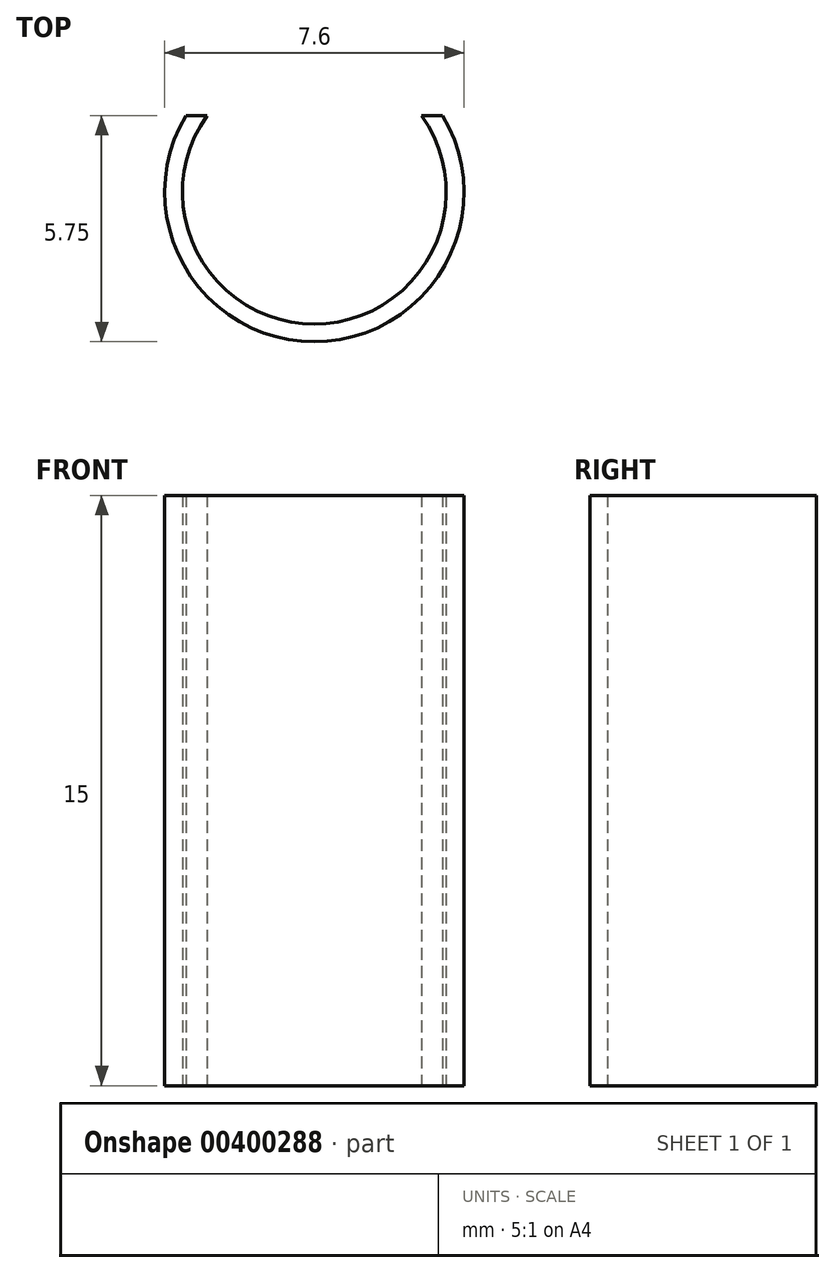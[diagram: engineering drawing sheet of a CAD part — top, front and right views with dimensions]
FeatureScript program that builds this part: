
annotation { "Feature Type Name" : "Feature", "Feature Type Description" : "" }
export const myFeature = defineFeature(function(context is Context, id is Id, definition is map)
    precondition{}
    {
        {
            var Q0;
            Q0=qCreatedBy(makeId("Top.planeOp"),FACE);
            var sketch = newSketch(context, id + "F0", { "sketchPlane" : qUnion([Q0])});
            skCircle(sketch, "E0", {"center": v(0, 0) * mm, "radius": 3.35 * mm});
            skCircle(sketch, "E1", {"center": v(0, 0) * mm, "radius": 3.8 * mm});
            skLineSegment(sketch, "E2.bottom", {"start": v(-6.23, 6.68) * mm, "end": v(9.66, 6.68) * mm});
            skLineSegment(sketch, "E2.top", {"start": v(-6.23, 1.95) * mm, "end": v(9.66, 1.95) * mm});
            skLineSegment(sketch, "E2.left", {"start": v(-6.23, 6.68) * mm, "end": v(-6.23, 1.95) * mm});
            skLineSegment(sketch, "E2.right", {"start": v(9.66, 6.68) * mm, "end": v(9.66, 1.95) * mm});
            skLineSegment(sketch, "E3", {"start": v(0, -3.35) * mm, "end": v(-7.72, -3.35) * mm, "construction": true});
            skSolve(sketch);
        }
        {
            var Q0;
            {var subQ0=sQuery(id+"F0.wireOp",EDGE,"E2.top");var subQ1=sQuery(id+"F0.wireOp",EDGE,"E0");var subQ2=makeQuery(id+"F0.imprint","INTERSECT",VERTEX,{"disambiguationData":[OD(0.0)],"derivedFrom":[subQ1,subQ0]});Q0=makeQuery(id+"F0.imprint","IMPRINT",FACE,{"disambiguationData":[TD([[makeQuery(id+"F0.imprint","IMPRINT",EDGE,{"disambiguationData":[TD([[subQ2,-1.0]])],"derivedFrom":subQ1}),-1.0]])]});}
            extrude(context, id + "F1", {"entities" : qUnion([Q0]), "depth" : 15 * mm});
        }
    });
